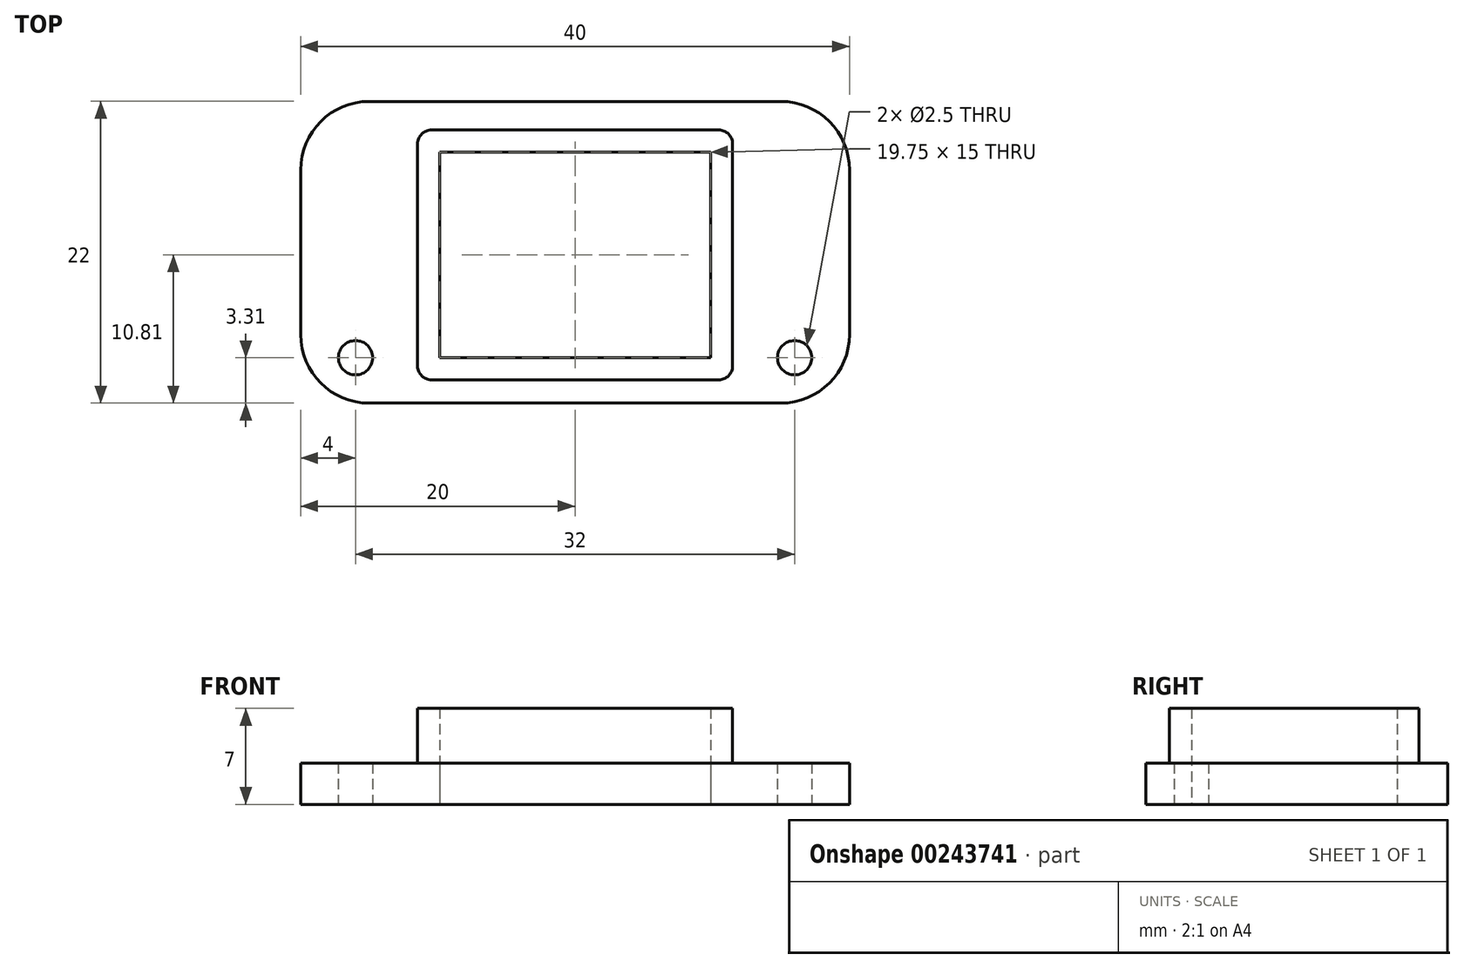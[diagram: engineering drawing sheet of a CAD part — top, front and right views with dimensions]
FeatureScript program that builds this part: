
annotation { "Feature Type Name" : "Feature", "Feature Type Description" : "" }
export const myFeature = defineFeature(function(context is Context, id is Id, definition is map)
    precondition{}
    {
        {
            var Q0;
            Q0=qCreatedBy(makeId("Top.planeOp"),FACE);
            var sketch = newSketch(context, id + "F0", { "sketchPlane" : qUnion([Q0])});
            skCircle(sketch, "E0", {"center": v(16, 0) * mm, "radius": 1.25 * mm});
            skCircle(sketch, "E1.MirrorC", {"center": v(-16, 0) * mm, "radius": 1.25 * mm});
            skLineSegment(sketch, "E2", {"start": v(0, -3.31) * mm, "end": v(20, -3.31) * mm});
            skLineSegment(sketch, "E3", {"start": v(20, -3.31) * mm, "end": v(20, 18.69) * mm});
            skLineSegment(sketch, "E4", {"start": v(20, 18.69) * mm, "end": v(0, 18.69) * mm});
            skLineSegment(sketch, "E5.bottom", {"start": v(9.87, 0) * mm, "end": v(-9.88, 0) * mm});
            skLineSegment(sketch, "E5.top", {"start": v(9.88, 15) * mm, "end": v(-9.87, 15) * mm});
            skLineSegment(sketch, "E5.left", {"start": v(9.88, 0) * mm, "end": v(9.88, 15) * mm});
            skLineSegment(sketch, "E5.right", {"start": v(-9.88, 0) * mm, "end": v(-9.87, 15) * mm});
            skPoint(sketch, "E5.middle", {"position": v(0, 7.5) * mm});
            skLineSegment(sketch, "E6.MirrorCS", {"start": v(-20, 18.69) * mm, "end": v(0, 18.69) * mm});
            skLineSegment(sketch, "E7.MirrorCS", {"start": v(-20, -3.31) * mm, "end": v(-20, 18.69) * mm});
            skLineSegment(sketch, "E8.MirrorCS", {"start": v(0, -3.31) * mm, "end": v(-20, -3.31) * mm});
            skSolve(sketch);
        }
        {
            var Q0;
            Q0 = qSketchRegion(id + "F0", true);
            extrude(context, id + "F1", {"entities" : qUnion([Q0]), "depth" : 3 * mm});
        }
        {
            var Q0;
            Q0=makeQuery(id+"F1.opExtrude","CAP_FACE",FACE,{"disambiguationData":[OSD([sQuery(id+"F0.wireOp",EDGE,"E0"),sQuery(id+"F0.wireOp",EDGE,"E1.MirrorC"),sQuery(id+"F0.wireOp",EDGE,"E2"),sQuery(id+"F0.wireOp",EDGE,"E3"),sQuery(id+"F0.wireOp",EDGE,"E4"),sQuery(id+"F0.wireOp",EDGE,"E5.bottom"),sQuery(id+"F0.wireOp",EDGE,"E5.top"),sQuery(id+"F0.wireOp",EDGE,"E5.left"),sQuery(id+"F0.wireOp",EDGE,"E5.right"),sQuery(id+"F0.wireOp",EDGE,"E6.MirrorCS"),sQuery(id+"F0.wireOp",EDGE,"E7.MirrorCS"),sQuery(id+"F0.wireOp",EDGE,"E8.MirrorCS")])],"isStart":false});
            var sketch = newSketch(context, id + "F2", { "sketchPlane" : qUnion([Q0])});
            skLineSegment(sketch, "E9.bottom", {"start": v(11.48, -1.61) * mm, "end": v(-11.48, -1.61) * mm});
            skLineSegment(sketch, "E9.top", {"start": v(11.48, 16.6) * mm, "end": v(-11.48, 16.6) * mm});
            skLineSegment(sketch, "E9.left", {"start": v(11.47, -1.61) * mm, "end": v(11.48, 16.6) * mm});
            skLineSegment(sketch, "E9.right", {"start": v(-11.48, -1.61) * mm, "end": v(-11.47, 16.6) * mm});
            skPoint(sketch, "E9.middle", {"position": v(0, 7.5) * mm});
            skPoint(sketch, "E9.middle.positionSnap0", {"position": v(0, 15) * mm});
            skPoint(sketch, "E9.centerSnap0", {"position": v(0, 15) * mm});
            skLineSegment(sketch, "E10.bottom", {"start": v(9.87, 0) * mm, "end": v(-9.87, 0) * mm});
            skLineSegment(sketch, "E10.top", {"start": v(9.87, 14.99) * mm, "end": v(-9.87, 14.99) * mm});
            skLineSegment(sketch, "E10.left", {"start": v(9.87, 0) * mm, "end": v(9.87, 14.99) * mm});
            skLineSegment(sketch, "E10.right", {"start": v(-9.87, 0) * mm, "end": v(-9.87, 14.99) * mm});
            skSolve(sketch);
        }
        {
            var Q0;
            Q0 = qSketchRegion(id + "F2", true);
            extrude(context, id + "F3", {"entities" : qUnion([Q0]), "operationType" : NewBodyOperationType.ADD, "depth" : 4 * mm});
        }
        {
            var Q0;
            Q0=makeQuery(id+"F1.opExtrude","SWEPT_EDGE",EDGE,{"disambiguationData":[OSD([sQuery(id+"F0.wireOp",EDGE,"E6.MirrorCS"),sQuery(id+"F0.wireOp",EDGE,"E7.MirrorCS")])]});
            var Q1;
            Q1=makeQuery(id+"F1.opExtrude","SWEPT_EDGE",EDGE,{"disambiguationData":[OSD([sQuery(id+"F0.wireOp",EDGE,"E3"),sQuery(id+"F0.wireOp",EDGE,"E4")])]});
            var Q2;
            Q2=makeQuery(id+"F1.opExtrude","SWEPT_EDGE",EDGE,{"disambiguationData":[OSD([sQuery(id+"F0.wireOp",EDGE,"E7.MirrorCS"),sQuery(id+"F0.wireOp",EDGE,"E8.MirrorCS")])]});
            var Q3;
            Q3=makeQuery(id+"F1.opExtrude","SWEPT_EDGE",EDGE,{"disambiguationData":[OSD([sQuery(id+"F0.wireOp",EDGE,"E2"),sQuery(id+"F0.wireOp",EDGE,"E3")])]});
            fillet(context, id + "F4", {"entities" : qUnion([Q0, Q1, Q2, Q3]), "radius" : 5 * mm, "tangentPropagation" : true, "allowEdgeOverflow" : false});
        }
        {
            var Q0;
            Q0=makeQuery(id+"F3.opExtrude","CAP_EDGE",EDGE,{"disambiguationData":[OSD([sQuery(id+"F2.wireOp",EDGE,"E9.top")])],"isStart":true});
            var Q1;
            Q1=makeQuery(id+"F3.opExtrude","CAP_EDGE",EDGE,{"disambiguationData":[OSD([sQuery(id+"F2.wireOp",EDGE,"E9.right")])],"isStart":true});
            var Q2;
            Q2=makeQuery(id+"F3.opExtrude","CAP_EDGE",EDGE,{"disambiguationData":[OSD([sQuery(id+"F2.wireOp",EDGE,"E9.bottom")])],"isStart":true});
            var Q3;
            Q3=makeQuery(id+"F3.opExtrude","CAP_EDGE",EDGE,{"disambiguationData":[OSD([sQuery(id+"F2.wireOp",EDGE,"E9.left")])],"isStart":true});
            var Q4;
            Q4=makeQuery(id+"F3.opExtrude","SWEPT_EDGE",EDGE,{"disambiguationData":[OSD([sQuery(id+"F2.wireOp",EDGE,"E9.bottom"),sQuery(id+"F2.wireOp",EDGE,"E9.left")])]});
            var Q5;
            Q5=makeQuery(id+"F3.opExtrude","SWEPT_EDGE",EDGE,{"disambiguationData":[OSD([sQuery(id+"F2.wireOp",EDGE,"E9.bottom"),sQuery(id+"F2.wireOp",EDGE,"E9.right")])]});
            var Q6;
            Q6=makeQuery(id+"F3.opExtrude","SWEPT_EDGE",EDGE,{"disambiguationData":[OSD([sQuery(id+"F2.wireOp",EDGE,"E9.top"),sQuery(id+"F2.wireOp",EDGE,"E9.left")])]});
            var Q7;
            Q7=makeQuery(id+"F3.opExtrude","SWEPT_EDGE",EDGE,{"disambiguationData":[OSD([sQuery(id+"F2.wireOp",EDGE,"E9.top"),sQuery(id+"F2.wireOp",EDGE,"E9.right")])]});
            fillet(context, id + "F5", {"entities" : qUnion([Q0, Q1, Q2, Q3, Q4, Q5, Q6, Q7]), "radius" : 1 * mm, "tangentPropagation" : true, "allowEdgeOverflow" : false});
        }
    });
